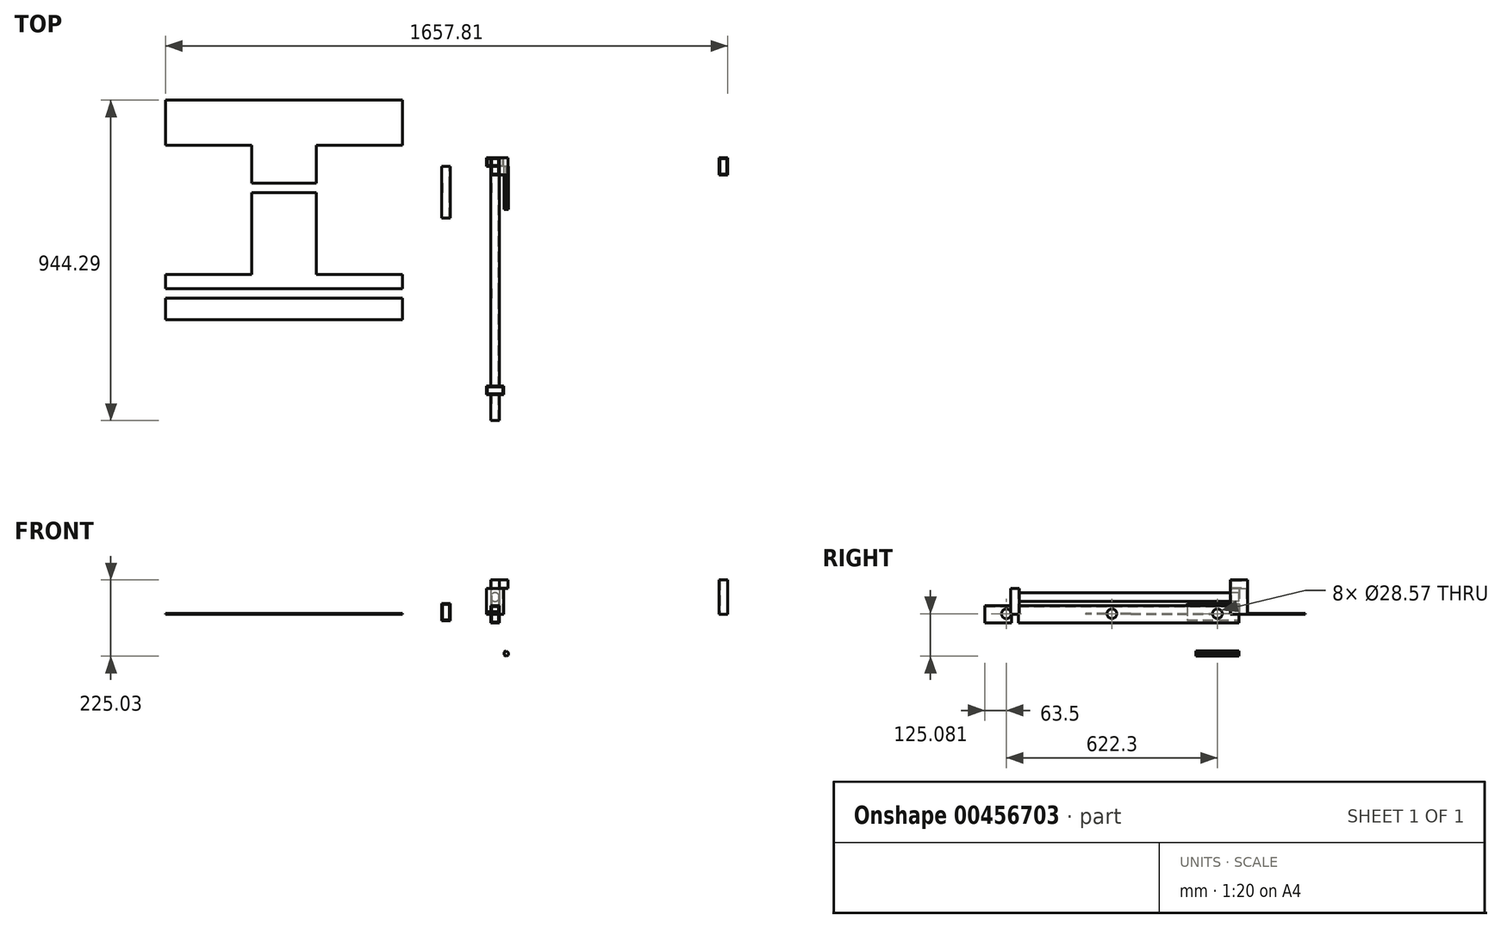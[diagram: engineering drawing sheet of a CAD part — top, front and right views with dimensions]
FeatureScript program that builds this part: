
annotation { "Feature Type Name" : "Feature", "Feature Type Description" : "" }
export const myFeature = defineFeature(function(context is Context, id is Id, definition is map)
    precondition{}
    {
        {
            assignVariable(context, id + "F0", {"name" : "chassis_width", "anyValue" : 27.5});
        }
        {
            var Q0;
            Q0=qCreatedBy(makeId("Front.planeOp"),FACE);
            var sketch = newSketch(context, id + "F1", { "sketchPlane" : qUnion([Q0])});
            skLineSegment(sketch, "E0.bottom", {"start": v(-12.7, 25.4) * mm, "end": v(12.7, 25.4) * mm});
            skLineSegment(sketch, "E0.top", {"start": v(-12.7, -25.4) * mm, "end": v(12.7, -25.4) * mm});
            skLineSegment(sketch, "E0.left", {"start": v(-12.7, 25.4) * mm, "end": v(-12.7, -25.4) * mm});
            skLineSegment(sketch, "E0.right", {"start": v(12.7, 25.4) * mm, "end": v(12.7, -25.4) * mm});
            skPoint(sketch, "E0.middle", {"position": v(0, 0) * mm});
            skLineSegment(sketch, "E1.0", {"start": v(-10.41, 23.11) * mm, "end": v(10.41, 23.11) * mm});
            skLineSegment(sketch, "E1.1", {"start": v(-10.41, 23.11) * mm, "end": v(-10.41, -23.11) * mm});
            skLineSegment(sketch, "E1.2", {"start": v(-10.41, -23.11) * mm, "end": v(10.41, -23.11) * mm});
            skLineSegment(sketch, "E1.3", {"start": v(10.41, 23.11) * mm, "end": v(10.41, -23.11) * mm});
            skSolve(sketch);
        }
        {
            var Q0;
            Q0=makeQuery(id+"F1.imprint","IMPRINT",FACE,{"disambiguationData":[TD([[makeQuery(id+"F1.imprint","IMPRINT",EDGE,{"derivedFrom":sQuery(id+"F1.wireOp",EDGE,"E0.bottom")}),-1.0]])]});
            extrude(context, id + "F2", {"entities" : qUnion([Q0]), "depth" : 749.3 * mm});
        }
        {
            var Q0;
            Q0=qCreatedBy(makeId("Front.planeOp"),FACE);
            var sketch = newSketch(context, id + "F3", { "sketchPlane" : qUnion([Q0])});
            skLineSegment(sketch, "E2.bottom", {"start": v(-157.28, 31.83) * mm, "end": v(-131.88, 31.83) * mm});
            skLineSegment(sketch, "E2.top", {"start": v(-157.28, -18.97) * mm, "end": v(-131.88, -18.97) * mm});
            skLineSegment(sketch, "E2.left", {"start": v(-157.28, 31.83) * mm, "end": v(-157.28, -18.97) * mm});
            skLineSegment(sketch, "E2.right", {"start": v(-131.88, 31.83) * mm, "end": v(-131.88, -18.97) * mm});
            skPoint(sketch, "E2.middle", {"position": v(-144.58, 6.43) * mm});
            skLineSegment(sketch, "E3.0", {"start": v(-155, 29.54) * mm, "end": v(-134.17, 29.54) * mm});
            skLineSegment(sketch, "E3.1", {"start": v(-155, 29.54) * mm, "end": v(-155, -16.68) * mm});
            skLineSegment(sketch, "E3.2", {"start": v(-155, -16.68) * mm, "end": v(-134.17, -16.68) * mm});
            skLineSegment(sketch, "E3.3", {"start": v(-134.17, 29.54) * mm, "end": v(-134.17, -16.68) * mm});
            skSolve(sketch);
        }
        {
            var Q0;
            Q0=makeQuery(id+"F3.imprint","IMPRINT",FACE,{"disambiguationData":[TD([[makeQuery(id+"F3.imprint","IMPRINT",EDGE,{"derivedFrom":sQuery(id+"F3.wireOp",EDGE,"E2.bottom")}),-1.0]])]});
            extrude(context, id + "F4", {"entities" : qUnion([Q0]), "depth" : 152.4 * mm});
        }
        {
            var Q0;
            Q0=qCreatedBy(makeId("Top.planeOp"),FACE);
            var sketch = newSketch(context, id + "F5", { "sketchPlane" : qUnion([Q0])});
            skLineSegment(sketch, "E4.bottom", {"start": v(-972, 195) * mm, "end": v(-273.5, 195) * mm});
            skLineSegment(sketch, "E4.top", {"start": v(-972, -452.7) * mm, "end": v(-273.5, -452.7) * mm});
            skLineSegment(sketch, "E4.left", {"start": v(-972, 195) * mm, "end": v(-972, -452.7) * mm});
            skLineSegment(sketch, "E4.right", {"start": v(-273.5, 195) * mm, "end": v(-273.5, -452.7) * mm});
            skLineSegment(sketch, "E5", {"start": v(0, 0) * mm, "end": v(-273.5, -452.7) * mm, "construction": true});
            skLineSegment(sketch, "E6.bottom", {"start": v(-273.5, -319.36) * mm, "end": v(-527.5, -319.36) * mm});
            skLineSegment(sketch, "E6.top", {"start": v(-273.5, 61.64) * mm, "end": v(-527.5, 61.64) * mm});
            skLineSegment(sketch, "E6.left", {"start": v(-273.5, -319.36) * mm, "end": v(-273.5, 61.64) * mm});
            skLineSegment(sketch, "E6.right", {"start": v(-527.5, -319.36) * mm, "end": v(-527.5, 61.64) * mm});
            skLineSegment(sketch, "E7.bottom", {"start": v(-972, -319.36) * mm, "end": v(-718, -319.36) * mm});
            skLineSegment(sketch, "E7.top", {"start": v(-972, 61.64) * mm, "end": v(-718, 61.64) * mm});
            skLineSegment(sketch, "E7.left", {"start": v(-972, -319.36) * mm, "end": v(-972, 61.64) * mm});
            skLineSegment(sketch, "E7.right", {"start": v(-718, -319.36) * mm, "end": v(-718, 61.64) * mm});
            skSolve(sketch);
        }
        {
            var Q0;
            Q0=makeQuery(id+"F5.imprint","IMPRINT",FACE,{"disambiguationData":[TD([[makeQuery(id+"F5.imprint","IMPRINT",EDGE,{"derivedFrom":sQuery(id+"F5.wireOp",EDGE,"E4.bottom")}),-1.0]])]});
            extrude(context, id + "F6", {"entities" : qUnion([Q0]), "depth" : 3.17 * mm});
        }
        {
            var Q0;
            Q0=qCreatedBy(makeId("Right.planeOp"),FACE);
            var sketch = newSketch(context, id + "F7", { "sketchPlane" : qUnion([Q0])});
            skLineSegment(sketch, "E8.bottom", {"start": v(-673.1, 76.2) * mm, "end": v(-647.7, 76.2) * mm});
            skLineSegment(sketch, "E8.top", {"start": v(-673.1, 0) * mm, "end": v(-647.7, 0) * mm});
            skLineSegment(sketch, "E8.left", {"start": v(-673.1, 76.2) * mm, "end": v(-673.1, 0) * mm});
            skLineSegment(sketch, "E8.right", {"start": v(-647.7, 76.2) * mm, "end": v(-647.7, 0) * mm});
            skLineSegment(sketch, "E9.bottom", {"start": v(0, 76.2) * mm, "end": v(25.4, 76.2) * mm});
            skLineSegment(sketch, "E9.top", {"start": v(0, 0) * mm, "end": v(25.4, 0) * mm});
            skLineSegment(sketch, "E9.left", {"start": v(0, 76.2) * mm, "end": v(0, 0) * mm});
            skLineSegment(sketch, "E9.right", {"start": v(25.4, 76.2) * mm, "end": v(25.4, 0) * mm});
            skLineSegment(sketch, "E10.bottom", {"start": v(-647.7, 63.5) * mm, "end": v(0, 63.5) * mm});
            skLineSegment(sketch, "E10.top", {"start": v(-647.7, 38.1) * mm, "end": v(0, 38.1) * mm});
            skLineSegment(sketch, "E10.left", {"start": v(-647.7, 63.5) * mm, "end": v(-647.7, 38.1) * mm});
            skLineSegment(sketch, "E10.right", {"start": v(0, 63.5) * mm, "end": v(0, 38.1) * mm});
            skLineSegment(sketch, "E11", {"start": v(-647.7, 50.8) * mm, "end": v(0, 50.8) * mm});
            skLineSegment(sketch, "E12", {"start": v(0, 76.2) * mm, "end": v(-647.7, 76.2) * mm, "construction": true});
            skSolve(sketch);
        }
        {
            var Q0;
            {var subQ1=sQuery(id+"F7.wireOp",EDGE,"E8.bottom");Q0=makeQuery(id+"F7.imprint","IMPRINT",FACE,{"disambiguationData":[TD([[makeQuery(id+"F7.imprint","IMPRINT",EDGE,{"derivedFrom":subQ1}),-1.0]])]});}
            var Q1;
            {var subQ3=sQuery(id+"F7.wireOp",EDGE,"E9.bottom");Q1=makeQuery(id+"F7.imprint","IMPRINT",FACE,{"disambiguationData":[TD([[makeQuery(id+"F7.imprint","IMPRINT",EDGE,{"derivedFrom":subQ3}),-1.0]])]});}
            extrude(context, id + "F8", {"entities" : qUnion([Q0, Q1]), "endBound" : BoundingType.SYMMETRIC, "depth" : 50.8 * mm});
        }
        {
            var Q0;
            Q0=makeQuery(id+"F7.imprint","IMPRINT",FACE,{"disambiguationData":[TD([[makeQuery(id+"F7.imprint","IMPRINT",EDGE,{"derivedFrom":sQuery(id+"F7.wireOp",EDGE,"E10.bottom")}),-1.0]])]});
            var Q1;
            Q1=sQuery(id+"F7.wireOp",EDGE,"E11");
            revolve(context, id + "F9", {"operationType" : NewBodyOperationType.ADD, "entities" : qUnion([Q0]), "axis" : qUnion([Q1]), "revolveType" : RevolveType.FULL});
        }
        {
            var Q0;
            Q0=makeQuery(id+"F8.opExtrude","SWEPT_FACE",FACE,{"disambiguationData":[OSD([sQuery(id+"F7.wireOp",EDGE,"E8.bottom")])]});
            var sketch = newSketch(context, id + "F10", { "sketchPlane" : qUnion([Q0])});
            skLineSegment(sketch, "E13.bottom", {"start": v(23.11, -670.81) * mm, "end": v(-23.11, -670.81) * mm});
            skLineSegment(sketch, "E13.top", {"start": v(23.11, -649.99) * mm, "end": v(-23.11, -649.99) * mm});
            skLineSegment(sketch, "E13.left", {"start": v(23.11, -670.81) * mm, "end": v(23.11, -649.99) * mm});
            skLineSegment(sketch, "E13.right", {"start": v(-23.11, -670.81) * mm, "end": v(-23.11, -649.99) * mm});
            skSolve(sketch);
        }
        {
            var Q0;
            Q0=makeQuery(id+"F10.imprint","IMPRINT",FACE,{"disambiguationData":[TD([[makeQuery(id+"F10.imprint","IMPRINT",EDGE,{"derivedFrom":sQuery(id+"F10.wireOp",EDGE,"E13.bottom")}),-1.0]])]});
            extrude(context, id + "F11", {"entities" : qUnion([Q0]), "operationType" : NewBodyOperationType.REMOVE, "endBound" : BoundingType.THROUGH_ALL, "oppositeDirection" : true, "depth" : 25.4 * mm});
        }
        {
            var Q0;
            Q0=makeQuery(id+"F8.opExtrude","SWEPT_FACE",FACE,{"disambiguationData":[OSD([sQuery(id+"F7.wireOp",EDGE,"E9.bottom")])]});
            var sketch = newSketch(context, id + "F12", { "sketchPlane" : qUnion([Q0])});
            skLineSegment(sketch, "E14.bottom", {"start": v(-23.11, 2.29) * mm, "end": v(23.11, 2.29) * mm});
            skLineSegment(sketch, "E14.top", {"start": v(-23.11, 23.11) * mm, "end": v(23.11, 23.11) * mm});
            skLineSegment(sketch, "E14.left", {"start": v(-23.11, 2.29) * mm, "end": v(-23.11, 23.11) * mm});
            skLineSegment(sketch, "E14.right", {"start": v(23.11, 2.29) * mm, "end": v(23.11, 23.11) * mm});
            skSolve(sketch);
        }
        {
            var Q0;
            Q0=makeQuery(id+"F12.imprint","IMPRINT",FACE,{"disambiguationData":[TD([[makeQuery(id+"F12.imprint","IMPRINT",EDGE,{"derivedFrom":sQuery(id+"F12.wireOp",EDGE,"E14.bottom")}),1.0]])]});
            extrude(context, id + "F13", {"entities" : qUnion([Q0]), "operationType" : NewBodyOperationType.REMOVE, "endBound" : BoundingType.THROUGH_ALL, "oppositeDirection" : true, "depth" : 25.4 * mm});
        }
        {
            var Q0;
            Q0=makeQuery(id+"F2.opExtrude","SWEPT_FACE",FACE,{"disambiguationData":[OSD([sQuery(id+"F1.wireOp",EDGE,"E0.right")])]});
            var sketch = newSketch(context, id + "F14", { "sketchPlane" : qUnion([Q0])});
            skLineSegment(sketch, "E15", {"start": v(-749.3, 1.65) * mm, "end": v(0, 1.65) * mm, "construction": true});
            skCircle(sketch, "E16", {"center": v(-685.8, 1.65) * mm, "radius": 14.29 * mm});
            skCircle(sketch, "E17", {"center": v(-374.65, 1.65) * mm, "radius": 14.29 * mm});
            skCircle(sketch, "E18", {"center": v(-63.5, 1.65) * mm, "radius": 14.29 * mm});
            skSolve(sketch);
        }
        {
            var Q0;
            Q0=makeQuery(id+"F14.imprint","IMPRINT",FACE,{"disambiguationData":[TD([[makeQuery(id+"F14.imprint","IMPRINT",EDGE,{"derivedFrom":sQuery(id+"F14.wireOp",EDGE,"E16")}),1.0]])]});
            var Q1;
            Q1=makeQuery(id+"F14.imprint","IMPRINT",FACE,{"disambiguationData":[TD([[makeQuery(id+"F14.imprint","IMPRINT",EDGE,{"derivedFrom":sQuery(id+"F14.wireOp",EDGE,"E17")}),1.0]])]});
            var Q2;
            Q2=makeQuery(id+"F14.imprint","IMPRINT",FACE,{"disambiguationData":[TD([[makeQuery(id+"F14.imprint","IMPRINT",EDGE,{"derivedFrom":sQuery(id+"F14.wireOp",EDGE,"E18")}),1.0]])]});
            extrude(context, id + "F15", {"entities" : qUnion([Q0, Q1, Q2]), "operationType" : NewBodyOperationType.REMOVE, "endBound" : BoundingType.THROUGH_ALL, "oppositeDirection" : true, "depth" : 25.4 * mm});
        }
        {
            var Q0;
            Q0=qCreatedBy(makeId("Top.planeOp"),FACE);
            var sketch = newSketch(context, id + "F16", { "sketchPlane" : qUnion([Q0])});
            skLineSegment(sketch, "E19.bottom", {"start": v(-10.16, 22.86) * mm, "end": v(10.16, 22.86) * mm});
            skLineSegment(sketch, "E19.top", {"start": v(-10.16, -22.86) * mm, "end": v(10.16, -22.86) * mm});
            skLineSegment(sketch, "E19.left", {"start": v(-10.16, 22.86) * mm, "end": v(-10.16, -22.86) * mm});
            skLineSegment(sketch, "E19.right", {"start": v(10.16, 22.86) * mm, "end": v(10.16, -22.86) * mm});
            skPoint(sketch, "E19.middle", {"position": v(0, 0) * mm});
            skLineSegment(sketch, "E20.bottom", {"start": v(-12.7, 25.4) * mm, "end": v(12.7, 25.4) * mm});
            skLineSegment(sketch, "E20.top", {"start": v(-12.7, -25.4) * mm, "end": v(12.7, -25.4) * mm});
            skLineSegment(sketch, "E20.left", {"start": v(-12.7, 25.4) * mm, "end": v(-12.7, -25.4) * mm});
            skLineSegment(sketch, "E20.right", {"start": v(12.7, 25.4) * mm, "end": v(12.7, -25.4) * mm});
            skLineSegment(sketch, "E21", {"start": v(336.55, 63.25) * mm, "end": v(336.55, -48.65) * mm, "construction": true});
            skLineSegment(sketch, "E22.MirrorCS", {"start": v(683.26, 22.86) * mm, "end": v(662.94, 22.86) * mm});
            skLineSegment(sketch, "E23.MirrorCS", {"start": v(685.8, 25.4) * mm, "end": v(660.4, 25.4) * mm});
            skLineSegment(sketch, "E24.MirrorCS", {"start": v(660.4, 25.4) * mm, "end": v(660.4, -25.4) * mm});
            skPoint(sketch, "E25.MirrorP", {"position": v(673.1, 0) * mm});
            skLineSegment(sketch, "E26.MirrorCS", {"start": v(683.26, -22.86) * mm, "end": v(662.94, -22.86) * mm});
            skLineSegment(sketch, "E27.MirrorCS", {"start": v(685.8, -25.4) * mm, "end": v(660.4, -25.4) * mm});
            skLineSegment(sketch, "E28.MirrorCS", {"start": v(685.8, 25.4) * mm, "end": v(685.8, -25.4) * mm});
            skLineSegment(sketch, "E29.MirrorCS", {"start": v(683.26, 22.86) * mm, "end": v(683.26, -22.86) * mm});
            skLineSegment(sketch, "E30.MirrorCS", {"start": v(662.94, 22.86) * mm, "end": v(662.94, -22.86) * mm});
            skSolve(sketch);
        }
        {
            var Q0;
            Q0=makeQuery(id+"F16.imprint","IMPRINT",FACE,{"disambiguationData":[TD([[makeQuery(id+"F16.imprint","IMPRINT",EDGE,{"derivedFrom":sQuery(id+"F16.wireOp",EDGE,"E19.bottom")}),1.0]])]});
            var Q1;
            Q1=makeQuery(id+"F16.imprint","IMPRINT",FACE,{"disambiguationData":[TD([[makeQuery(id+"F16.imprint","IMPRINT",EDGE,{"derivedFrom":sQuery(id+"F16.wireOp",EDGE,"E22.MirrorCS")}),-1.0]])]});
            extrude(context, id + "F17", {"entities" : qUnion([Q0, Q1]), "depth" : 101.6 * mm});
        }
        {
            var Q0;
            Q0=makeQuery(id+"F17.opExtrude","SWEPT_FACE",FACE,{"disambiguationData":[OSD([sQuery(id+"F16.wireOp",EDGE,"E20.right")])]});
            var sketch = newSketch(context, id + "F18", { "sketchPlane" : qUnion([Q0])});
            skLineSegment(sketch, "E31.0", {"start": v(-25.4, 101.6) * mm, "end": v(-25.4, 0) * mm});
            skLineSegment(sketch, "E32.0", {"start": v(25.4, 101.6) * mm, "end": v(-25.4, 101.6) * mm});
            skLineSegment(sketch, "E33.0", {"start": v(25.4, 101.6) * mm, "end": v(25.4, 0) * mm});
            skLineSegment(sketch, "E34", {"start": v(-25.4, 76.2) * mm, "end": v(25.4, 76.2) * mm});
            skLineSegment(sketch, "E35", {"start": v(25.4, 101.6) * mm, "end": v(-25.4, 76.2) * mm, "construction": true});
            skLineSegment(sketch, "E36.bottom", {"start": v(-22.86, 99.06) * mm, "end": v(22.86, 99.06) * mm});
            skLineSegment(sketch, "E36.top", {"start": v(-22.86, 78.74) * mm, "end": v(22.86, 78.74) * mm});
            skLineSegment(sketch, "E36.left", {"start": v(-22.86, 99.06) * mm, "end": v(-22.86, 78.74) * mm});
            skLineSegment(sketch, "E36.right", {"start": v(22.86, 99.06) * mm, "end": v(22.86, 78.74) * mm});
            skPoint(sketch, "E36.middle", {"position": v(0, 88.9) * mm});
            skSolve(sketch);
        }
        {
            var Q0;
            {var subQ1=sQuery(id+"F18.wireOp",EDGE,"E32.0");Q0=makeQuery(id+"F18.imprint","IMPRINT",FACE,{"disambiguationData":[TD([[makeQuery(id+"F18.imprint","IMPRINT",EDGE,{"derivedFrom":subQ1}),1.0]])]});}
            extrude(context, id + "F19", {"entities" : qUnion([Q0]), "depth" : (getVariable(context, 'chassis_width') - 2) * mm});
        }
        {
            var Q0;
            Q0=qCreatedBy(makeId("Front.planeOp"),FACE);
            var sketch = newSketch(context, id + "F20", { "sketchPlane" : qUnion([Q0])});
            skCircle(sketch, "E37.cCircle", {"center": v(33.3, -115.83) * mm, "radius": 7.61 * mm, "construction": true});
            skLineSegment(sketch, "E37.0", {"start": v(39.65, -120.03) * mm, "end": v(32.84, -123.43) * mm});
            skLineSegment(sketch, "E37.1", {"start": v(32.84, -123.43) * mm, "end": v(26.49, -119.23) * mm});
            skLineSegment(sketch, "E37.2", {"start": v(26.49, -119.23) * mm, "end": v(26.95, -111.63) * mm});
            skLineSegment(sketch, "E37.3", {"start": v(26.95, -111.63) * mm, "end": v(33.76, -108.23) * mm});
            skLineSegment(sketch, "E37.4", {"start": v(33.76, -108.23) * mm, "end": v(40.11, -112.43) * mm});
            skLineSegment(sketch, "E37.5", {"start": v(40.11, -112.43) * mm, "end": v(39.65, -120.03) * mm});
            skSolve(sketch);
        }
        {
            var Q0;
            Q0=makeQuery(id+"F20.imprint","IMPRINT",FACE,{"disambiguationData":[TD([[makeQuery(id+"F20.imprint","IMPRINT",EDGE,{"derivedFrom":sQuery(id+"F20.wireOp",EDGE,"E37.0")}),-1.0]])]});
            extrude(context, id + "F21", {"entities" : qUnion([Q0]), "depth" : 127 * mm});
        }
    });
